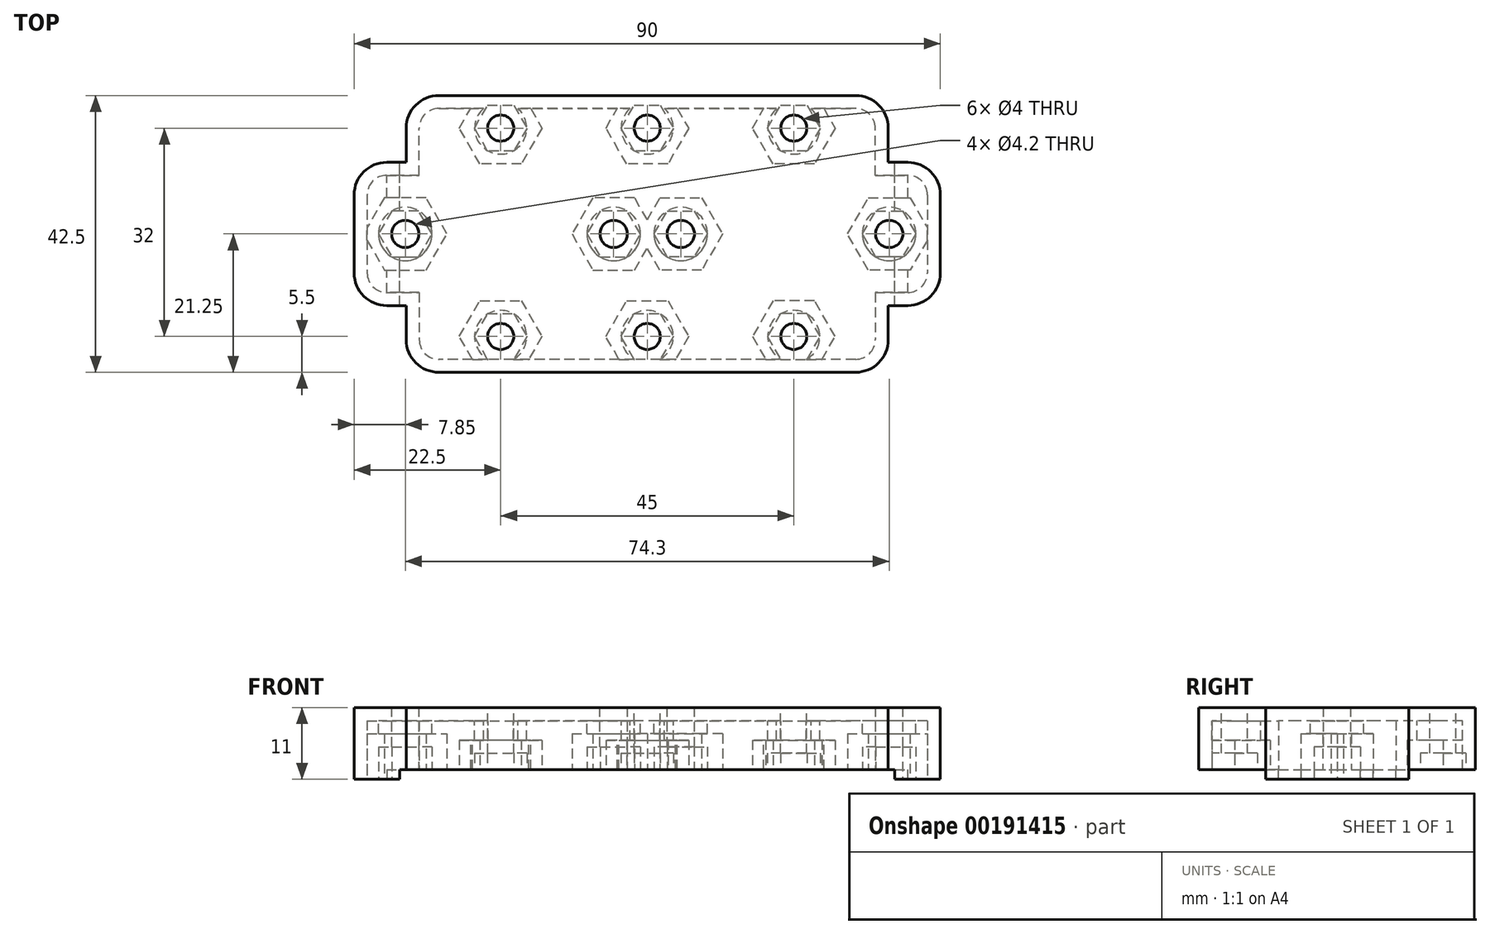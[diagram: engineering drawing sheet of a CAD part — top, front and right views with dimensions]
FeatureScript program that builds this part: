
annotation { "Feature Type Name" : "Feature", "Feature Type Description" : "" }
export const myFeature = defineFeature(function(context is Context, id is Id, definition is map)
    precondition{}
    {
        {
            var Q0;
            Q0=qCreatedBy(makeId("Top.planeOp"),FACE);
            var sketch = newSketch(context, id + "F0", { "sketchPlane" : qUnion([Q0])});
            skLineSegment(sketch, "E0.top", {"start": v(37, -37.5) * mm, "end": v(-37, -37.5) * mm});
            skLineSegment(sketch, "E0.left", {"start": v(45, -5.25) * mm, "end": v(45, -27.25) * mm});
            skLineSegment(sketch, "E0.right", {"start": v(-45, -5.25) * mm, "end": v(-45, -27.25) * mm});
            skPoint(sketch, "E0.middle", {"position": v(0, 0) * mm});
            skLineSegment(sketch, "E1", {"start": v(-37, 5) * mm, "end": v(37, 5) * mm});
            skPoint(sketch, "E0.bottom.end.orphan", {"position": v(-45, 37.5) * mm});
            skPoint(sketch, "E2.orphan", {"position": v(45, 37.5) * mm});
            skLineSegment(sketch, "E3.top", {"start": v(45, -5.25) * mm, "end": v(37, -5.25) * mm});
            skLineSegment(sketch, "E3.right", {"start": v(37, 5) * mm, "end": v(37, -5.25) * mm});
            skLineSegment(sketch, "E4", {"start": v(-45, -16.25) * mm, "end": v(45, -16.25) * mm, "construction": true});
            skLineSegment(sketch, "E5.MirrorCS", {"start": v(45, -27.25) * mm, "end": v(37, -27.25) * mm});
            skLineSegment(sketch, "E6.MirrorCS", {"start": v(37, -37.5) * mm, "end": v(37, -27.25) * mm});
            skLineSegment(sketch, "E7.MirrorCS", {"start": v(-45, -27.25) * mm, "end": v(-37, -27.25) * mm});
            skLineSegment(sketch, "E8.MirrorCS", {"start": v(-37, 5) * mm, "end": v(-37, -5.25) * mm});
            skLineSegment(sketch, "E9.MirrorCS", {"start": v(-45, -5.25) * mm, "end": v(-37, -5.25) * mm});
            skLineSegment(sketch, "E10.MirrorCS", {"start": v(-37, -37.5) * mm, "end": v(-37, -27.25) * mm});
            skPoint(sketch, "E11.orphan", {"position": v(45, 5) * mm});
            skPoint(sketch, "E12.MirrorCS.start.orphan", {"position": v(45, -37.5) * mm});
            skPoint(sketch, "E13.MirrorCS.start.orphan", {"position": v(-45, 5) * mm});
            skPoint(sketch, "E14.orphan", {"position": v(-45, -37.5) * mm});
            skSolve(sketch);
        }
        {
            var Q0;
            Q0=qSketchRegion(id+"F0",true);
            extrude(context, id + "F1", {"entities" : qUnion([Q0]), "depth" : 11 * mm});
        }
        {
            var Q0;
            {var subQ0=sQuery(id+"Ftu9CyJNp9XUoHb_1.wireOp",EDGE,"RhgawOvt-7kr6-Sdrn-dJV1-QJA8v9KPNXqK");var subQ1=sQuery(id+"FDzObh8OvUh78c8_1.wireOp",EDGE,"89ed7744-1fdc-4696-88ab-c0afdf2aee140.MirrorC");var subQ2=sQuery(id+"Ftu9CyJNp9XUoHb_1.wireOp",EDGE,"5e429970-d295-4fee-98a3-73d9fe4554250.MirrorC");var subQ3=sQuery(id+"FDzObh8OvUh78c8_1.wireOp",EDGE,"xi41FaaG-PnNu-ulyK-8lT2-qR5dbplvMgDO");var subQ4=sQuery(id+"F0.wireOp",EDGE,"E0.right");var subQ5=sQuery(id+"F0.wireOp",EDGE,"E0.left");Q0=makeQuery(id+"FwhSho8yxuuqSUd_1.boolean.opBoolean","SPLIT",FACE,{"disambiguationData":[TD([makeQuery(id+"F1.opExtrude","SWEPT_FACE",FACE,{"disambiguationData":[OSD([subQ5])]}),makeQuery(id+"F1.opExtrude","SWEPT_FACE",FACE,{"disambiguationData":[OSD([subQ4])]}),makeQuery(id+"FezKC2GjwbwwqvD_1.boolean.opBoolean","COPY",FACE,{"derivedFrom":makeQuery(id+"FezKC2GjwbwwqvD_1.opExtrude","SWEPT_FACE",FACE,{"disambiguationData":[OSD([subQ3])]})}),makeQuery(id+"FezKC2GjwbwwqvD_1.boolean.opBoolean","COPY",FACE,{"derivedFrom":makeQuery(id+"FezKC2GjwbwwqvD_1.opExtrude","CAP_FACE",FACE,{"disambiguationData":[OSD([subQ3])],"isStart":true})}),makeQuery(id+"FezKC2GjwbwwqvD_1.boolean.opBoolean","COPY",FACE,{"derivedFrom":makeQuery(id+"FezKC2GjwbwwqvD_1.opExtrude","CAP_FACE",FACE,{"disambiguationData":[OSD([subQ3])],"isStart":false})}),makeQuery(id+"FezKC2GjwbwwqvD_1.boolean.opBoolean","COPY",FACE,{"derivedFrom":makeQuery(id+"FezKC2GjwbwwqvD_1.opExtrude","SWEPT_FACE",FACE,{"disambiguationData":[OSD([subQ1])]})}),makeQuery(id+"FezKC2GjwbwwqvD_1.boolean.opBoolean","COPY",FACE,{"derivedFrom":makeQuery(id+"FezKC2GjwbwwqvD_1.opExtrude","CAP_FACE",FACE,{"disambiguationData":[OSD([subQ1])],"isStart":true})}),makeQuery(id+"FezKC2GjwbwwqvD_1.boolean.opBoolean","COPY",FACE,{"derivedFrom":makeQuery(id+"FezKC2GjwbwwqvD_1.opExtrude","CAP_FACE",FACE,{"disambiguationData":[OSD([subQ1])],"isStart":false})}),makeQuery(id+"Fv9pJnclqYY7mwX_1.boolean.opBoolean","COPY",FACE,{"derivedFrom":makeQuery(id+"Fv9pJnclqYY7mwX_1.opExtrude","SWEPT_FACE",FACE,{"disambiguationData":[OSD([subQ0])]})}),makeQuery(id+"Fv9pJnclqYY7mwX_1.boolean.opBoolean","COPY",FACE,{"derivedFrom":makeQuery(id+"Fv9pJnclqYY7mwX_1.opExtrude","CAP_FACE",FACE,{"disambiguationData":[OSD([subQ0])],"isStart":true})}),makeQuery(id+"Fv9pJnclqYY7mwX_1.boolean.opBoolean","COPY",FACE,{"derivedFrom":makeQuery(id+"Fv9pJnclqYY7mwX_1.opExtrude","CAP_FACE",FACE,{"disambiguationData":[OSD([subQ0])],"isStart":false})}),makeQuery(id+"Fv9pJnclqYY7mwX_1.boolean.opBoolean","COPY",FACE,{"derivedFrom":makeQuery(id+"Fv9pJnclqYY7mwX_1.opExtrude","SWEPT_FACE",FACE,{"disambiguationData":[OSD([subQ2])]})}),makeQuery(id+"Fv9pJnclqYY7mwX_1.boolean.opBoolean","COPY",FACE,{"derivedFrom":makeQuery(id+"Fv9pJnclqYY7mwX_1.opExtrude","CAP_FACE",FACE,{"disambiguationData":[OSD([subQ2])],"isStart":true})}),makeQuery(id+"Fv9pJnclqYY7mwX_1.boolean.opBoolean","COPY",FACE,{"derivedFrom":makeQuery(id+"Fv9pJnclqYY7mwX_1.opExtrude","CAP_FACE",FACE,{"disambiguationData":[OSD([subQ2])],"isStart":false})}),makeQuery(id+"FwhSho8yxuuqSUd_1.opExtrude","SWEPT_FACE",FACE,{"disambiguationData":[OSD([sQuery(id+"FwmFuU8kyHScjr7_1.wireOp",EDGE,"tpYNRhvY-wzzr-XPzG-ht9J-7hpqiQNTNnZq")])]}),makeQuery(id+"FwhSho8yxuuqSUd_1.opExtrude","SWEPT_FACE",FACE,{"disambiguationData":[OSD([sQuery(id+"FwmFuU8kyHScjr7_1.wireOp",EDGE,"4b7efacd-c033-4760-b56c-52784860be010.MirrorC")])]})])],"derivedFrom":makeQuery(id+"F1.opExtrude","CAP_FACE",FACE,{"disambiguationData":[OSD([sQuery(id+"F0.wireOp",EDGE,"E0.bottom"),sQuery(id+"F0.wireOp",EDGE,"E0.top"),subQ5,subQ4])],"isStart":false})});}
            var sketch = newSketch(context, id + "F2", { "sketchPlane" : qUnion([Q0])});
            skCircle(sketch, "E15", {"center": v(0, -32) * mm, "radius": 2 * mm});
            skCircle(sketch, "E16.MirrorC", {"center": v(-22.5, -32) * mm, "radius": 2 * mm});
            skCircle(sketch, "E17.MirrorC", {"center": v(22.5, -32) * mm, "radius": 2 * mm});
            skLineSegment(sketch, "E18", {"start": v(-45.52, -16) * mm, "end": v(58.52, -16) * mm});
            skCircle(sketch, "E19.MirrorC", {"center": v(-22.5, 0) * mm, "radius": 2 * mm});
            skCircle(sketch, "E20.MirrorC", {"center": v(0, 0) * mm, "radius": 2 * mm});
            skCircle(sketch, "E21.MirrorC", {"center": v(22.5, 0) * mm, "radius": 2 * mm});
            skSolve(sketch);
        }
        {
            var Q0;
            Q0=qSketchRegion(id+"F2",true);
            extrude(context, id + "F3", {"entities" : qUnion([Q0]), "operationType" : NewBodyOperationType.REMOVE, "endBound" : BoundingType.THROUGH_ALL, "oppositeDirection" : true, "depth" : 25 * mm});
        }
        {
            var Q0;
            Q0=makeQuery(id+"F1.opExtrude","CAP_FACE",FACE,{"disambiguationData":[OSD([sQuery(id+"F0.wireOp",EDGE,"E0.bottom"),sQuery(id+"F0.wireOp",EDGE,"E0.top"),sQuery(id+"F0.wireOp",EDGE,"E0.left"),sQuery(id+"F0.wireOp",EDGE,"E0.right")])],"isStart":true});
            var sketch = newSketch(context, id + "F4", { "sketchPlane" : qUnion([Q0])});
            skCircle(sketch, "E22.cCircle", {"center": v(-22.5, 32) * mm, "radius": 3.5 * mm, "construction": true});
            skLineSegment(sketch, "E22.0", {"start": v(-24.52, 35.5) * mm, "end": v(-20.48, 35.5) * mm});
            skLineSegment(sketch, "E22.1", {"start": v(-20.48, 35.5) * mm, "end": v(-18.46, 32) * mm});
            skLineSegment(sketch, "E22.2", {"start": v(-18.46, 32) * mm, "end": v(-20.48, 28.5) * mm});
            skLineSegment(sketch, "E22.3", {"start": v(-20.48, 28.5) * mm, "end": v(-24.52, 28.5) * mm});
            skLineSegment(sketch, "E22.4", {"start": v(-24.52, 28.5) * mm, "end": v(-26.54, 32) * mm});
            skLineSegment(sketch, "E22.5", {"start": v(-26.54, 32) * mm, "end": v(-24.52, 35.5) * mm});
            skPoint(sketch, "E22.0.midPoint", {"position": v(-22.5, 35.5) * mm});
            skLineSegment(sketch, "E23.MirrorCS", {"start": v(24.52, 35.5) * mm, "end": v(20.48, 35.5) * mm});
            skLineSegment(sketch, "E24.MirrorCS", {"start": v(26.54, 32) * mm, "end": v(24.52, 35.5) * mm});
            skLineSegment(sketch, "E25.MirrorCS", {"start": v(20.48, 28.5) * mm, "end": v(24.52, 28.5) * mm});
            skLineSegment(sketch, "E26.MirrorCS", {"start": v(18.46, 32) * mm, "end": v(20.48, 28.5) * mm});
            skCircle(sketch, "E27.MirrorC", {"center": v(22.5, 32) * mm, "radius": 3.5 * mm, "construction": true});
            skPoint(sketch, "E28.MirrorP", {"position": v(22.5, 35.5) * mm});
            skLineSegment(sketch, "E29.MirrorCS", {"start": v(24.52, 28.5) * mm, "end": v(26.54, 32) * mm});
            skLineSegment(sketch, "E30.MirrorCS", {"start": v(20.48, 35.5) * mm, "end": v(18.46, 32) * mm});
            skCircle(sketch, "E31.cCircle", {"center": v(0, 32) * mm, "radius": 3.5 * mm, "construction": true});
            skLineSegment(sketch, "E31.0", {"start": v(-2.02, 35.5) * mm, "end": v(2.02, 35.5) * mm});
            skLineSegment(sketch, "E31.1", {"start": v(2.02, 35.5) * mm, "end": v(4.04, 32) * mm});
            skLineSegment(sketch, "E31.2", {"start": v(4.04, 32) * mm, "end": v(2.02, 28.5) * mm});
            skLineSegment(sketch, "E31.3", {"start": v(2.02, 28.5) * mm, "end": v(-2.02, 28.5) * mm});
            skLineSegment(sketch, "E31.4", {"start": v(-2.02, 28.5) * mm, "end": v(-4.04, 32) * mm});
            skLineSegment(sketch, "E31.5", {"start": v(-4.04, 32) * mm, "end": v(-2.02, 35.5) * mm});
            skPoint(sketch, "E31.0.midPoint", {"position": v(0, 35.5) * mm});
            skCircle(sketch, "E32.cCircle", {"center": v(-22.5, 0) * mm, "radius": 3.5 * mm, "construction": true});
            skLineSegment(sketch, "E32.0", {"start": v(-24.52, 3.5) * mm, "end": v(-20.48, 3.5) * mm});
            skLineSegment(sketch, "E32.1", {"start": v(-20.48, 3.5) * mm, "end": v(-18.46, 0) * mm});
            skLineSegment(sketch, "E32.2", {"start": v(-18.46, 0) * mm, "end": v(-20.48, -3.5) * mm});
            skLineSegment(sketch, "E32.3", {"start": v(-20.48, -3.5) * mm, "end": v(-24.52, -3.5) * mm});
            skLineSegment(sketch, "E32.4", {"start": v(-24.52, -3.5) * mm, "end": v(-26.54, 0) * mm});
            skLineSegment(sketch, "E32.5", {"start": v(-26.54, 0) * mm, "end": v(-24.52, 3.5) * mm});
            skPoint(sketch, "E32.0.midPoint", {"position": v(-22.5, 3.5) * mm});
            skCircle(sketch, "E33.cCircle", {"center": v(0, 0) * mm, "radius": 3.5 * mm, "construction": true});
            skLineSegment(sketch, "E33.0", {"start": v(-2.02, 3.5) * mm, "end": v(2.02, 3.5) * mm});
            skLineSegment(sketch, "E33.1", {"start": v(2.02, 3.5) * mm, "end": v(4.04, 0) * mm});
            skLineSegment(sketch, "E33.2", {"start": v(4.04, 0) * mm, "end": v(2.02, -3.5) * mm});
            skLineSegment(sketch, "E33.3", {"start": v(2.02, -3.5) * mm, "end": v(-2.02, -3.5) * mm});
            skLineSegment(sketch, "E33.4", {"start": v(-2.02, -3.5) * mm, "end": v(-4.04, 0) * mm});
            skLineSegment(sketch, "E33.5", {"start": v(-4.04, 0) * mm, "end": v(-2.02, 3.5) * mm});
            skPoint(sketch, "E33.0.midPoint", {"position": v(0, 3.5) * mm});
            skCircle(sketch, "E34.cCircle", {"center": v(22.5, 0) * mm, "radius": 3.5 * mm, "construction": true});
            skLineSegment(sketch, "E34.0", {"start": v(20.48, 3.5) * mm, "end": v(24.52, 3.5) * mm});
            skLineSegment(sketch, "E34.1", {"start": v(24.52, 3.5) * mm, "end": v(26.54, 0) * mm});
            skLineSegment(sketch, "E34.2", {"start": v(26.54, 0) * mm, "end": v(24.52, -3.5) * mm});
            skLineSegment(sketch, "E34.3", {"start": v(24.52, -3.5) * mm, "end": v(20.48, -3.5) * mm});
            skLineSegment(sketch, "E34.4", {"start": v(20.48, -3.5) * mm, "end": v(18.46, 0) * mm});
            skLineSegment(sketch, "E34.5", {"start": v(18.46, 0) * mm, "end": v(20.48, 3.5) * mm});
            skPoint(sketch, "E34.0.midPoint", {"position": v(22.5, 3.5) * mm});
            skSolve(sketch);
        }
        {
            var Q0;
            Q0=qSketchRegion(id+"F4",true);
            extrude(context, id + "F5", {"entities" : qUnion([Q0]), "operationType" : NewBodyOperationType.REMOVE, "oppositeDirection" : true, "depth" : 4 * mm});
        }
        {
            var Q0;
            Q0=makeQuery(id+"F1.opExtrude","CAP_FACE",FACE,{"disambiguationData":[OSD([sQuery(id+"F0.wireOp",EDGE,"E0.top"),sQuery(id+"F0.wireOp",EDGE,"E0.left"),sQuery(id+"F0.wireOp",EDGE,"E0.right"),sQuery(id+"F0.wireOp",EDGE,"E1")])],"isStart":true});
            var sketch = newSketch(context, id + "F6", { "sketchPlane" : qUnion([Q0])});
            skLineSegment(sketch, "E35.bottom", {"start": v(38, 37.5) * mm, "end": v(-38, 37.5) * mm});
            skLineSegment(sketch, "E35.top", {"start": v(38, -5) * mm, "end": v(-38, -5) * mm});
            skLineSegment(sketch, "E35.left", {"start": v(38, 37.5) * mm, "end": v(38, -5) * mm});
            skLineSegment(sketch, "E35.right", {"start": v(-38, 37.5) * mm, "end": v(-38, -5) * mm});
            skPoint(sketch, "E35.middle", {"position": v(0, 16.25) * mm});
            skSolve(sketch);
        }
        {
            var Q0;
            Q0 = qSketchRegion(id + "F6", true);
            extrude(context, id + "F7", {"entities" : qUnion([Q0]), "operationType" : NewBodyOperationType.REMOVE, "oppositeDirection" : true, "depth" : 1.5 * mm});
        }
        {
            var Q0;
            Q0=makeQuery(id+"F1.opExtrude","SWEPT_EDGE",EDGE,{"disambiguationData":[OSD([sQuery(id+"F0.wireOp",EDGE,"E0.top"),sQuery(id+"F0.wireOp",EDGE,"E10.MirrorCS")])]});
            var Q1;
            Q1=makeQuery(id+"F1.opExtrude","SWEPT_EDGE",EDGE,{"disambiguationData":[OSD([sQuery(id+"F0.wireOp",EDGE,"E7.MirrorCS"),sQuery(id+"F0.wireOp",EDGE,"E0.right")])]});
            var Q2;
            Q2=makeQuery(id+"F1.opExtrude","SWEPT_EDGE",EDGE,{"disambiguationData":[OSD([sQuery(id+"F0.wireOp",EDGE,"E9.MirrorCS"),sQuery(id+"F0.wireOp",EDGE,"E0.right")])]});
            var Q3;
            Q3=makeQuery(id+"F1.opExtrude","SWEPT_EDGE",EDGE,{"disambiguationData":[OSD([sQuery(id+"F0.wireOp",EDGE,"E1"),sQuery(id+"F0.wireOp",EDGE,"E8.MirrorCS")])]});
            var Q4;
            Q4=makeQuery(id+"F1.opExtrude","SWEPT_EDGE",EDGE,{"disambiguationData":[OSD([sQuery(id+"F0.wireOp",EDGE,"E1"),sQuery(id+"F0.wireOp",EDGE,"E3.right")])]});
            var Q5;
            Q5=makeQuery(id+"F1.opExtrude","SWEPT_EDGE",EDGE,{"disambiguationData":[OSD([sQuery(id+"F0.wireOp",EDGE,"E0.left"),sQuery(id+"F0.wireOp",EDGE,"E3.top")])]});
            var Q6;
            Q6=makeQuery(id+"F1.opExtrude","SWEPT_EDGE",EDGE,{"disambiguationData":[OSD([sQuery(id+"F0.wireOp",EDGE,"E0.top"),sQuery(id+"F0.wireOp",EDGE,"E6.MirrorCS")])]});
            var Q7;
            Q7=makeQuery(id+"F1.opExtrude","SWEPT_EDGE",EDGE,{"disambiguationData":[OSD([sQuery(id+"F0.wireOp",EDGE,"E0.left"),sQuery(id+"F0.wireOp",EDGE,"E5.MirrorCS")])]});
            fillet(context, id + "F8", {"entities" : qUnion([Q0, Q1, Q2, Q3, Q4, Q5, Q6, Q7]), "radius" : 5 * mm, "tangentPropagation" : true, "allowEdgeOverflow" : false});
        }
        {
            var Q0;
            Q0=makeQuery(id+"F1.opExtrude","CAP_FACE",FACE,{"disambiguationData":[OSD([sQuery(id+"F0.wireOp",EDGE,"E0.top"),sQuery(id+"F0.wireOp",EDGE,"E0.left"),sQuery(id+"F0.wireOp",EDGE,"E1"),sQuery(id+"F0.wireOp",EDGE,"E3.top"),sQuery(id+"F0.wireOp",EDGE,"E3.right"),sQuery(id+"F0.wireOp",EDGE,"E5.MirrorCS"),sQuery(id+"F0.wireOp",EDGE,"E6.MirrorCS"),sQuery(id+"F0.wireOp",EDGE,"E7.MirrorCS"),sQuery(id+"F0.wireOp",EDGE,"E8.MirrorCS"),sQuery(id+"F0.wireOp",EDGE,"E9.MirrorCS"),sQuery(id+"F0.wireOp",EDGE,"E0.right"),sQuery(id+"F0.wireOp",EDGE,"E10.MirrorCS")])],"isStart":false});
            var sketch = newSketch(context, id + "F9", { "sketchPlane" : qUnion([Q0])});
            skPoint(sketch, "E36.middle", {"position": v(21.15, -16.25) * mm});
            skLineSegment(sketch, "E37", {"start": v(-45, -16.25) * mm, "end": v(54.06, -16.25) * mm, "construction": true});
            skPoint(sketch, "E38", {"position": v(45, -16.25) * mm});
            skCircle(sketch, "E39", {"center": v(37.15, -16.25) * mm, "radius": 2.1 * mm});
            skLineSegment(sketch, "E40", {"start": v(21.15, -16.25) * mm, "end": v(21.15, -48.47) * mm, "construction": true});
            skCircle(sketch, "E41.MirrorC", {"center": v(5.15, -16.25) * mm, "radius": 2.1 * mm});
            skLineSegment(sketch, "E42.MirrorCS", {"start": v(45, -16.25) * mm, "end": v(-54.06, -16.25) * mm, "construction": true});
            skCircle(sketch, "E43.MirrorC", {"center": v(-37.15, -16.25) * mm, "radius": 2.1 * mm});
            skPoint(sketch, "E44.MirrorP", {"position": v(-21.15, -16.25) * mm});
            skPoint(sketch, "E45.MirrorP", {"position": v(-45, -16.25) * mm});
            skLineSegment(sketch, "E46.MirrorCS", {"start": v(-21.15, -16.25) * mm, "end": v(-21.15, -48.47) * mm, "construction": true});
            skCircle(sketch, "E47.MirrorC", {"center": v(-5.15, -16.25) * mm, "radius": 2.1 * mm});
            skSolve(sketch);
        }
        {
            var Q0;
            Q0 = qSketchRegion(id + "F9", true);
            extrude(context, id + "F10", {"entities" : qUnion([Q0]), "operationType" : NewBodyOperationType.REMOVE, "endBound" : BoundingType.THROUGH_ALL, "oppositeDirection" : true, "depth" : 1 * mm});
        }
        {
            var Q0;
            {var subQ0=sQuery(id+"F0.wireOp",EDGE,"E7.MirrorCS");var subQ1=sQuery(id+"F0.wireOp",EDGE,"E9.MirrorCS");var subQ2=sQuery(id+"F0.wireOp",EDGE,"E0.right");Q0=makeQuery(id+"F7.boolean.opBoolean","SPLIT",FACE,{"disambiguationData":[TD([makeQuery(id+"F1.opExtrude","SWEPT_FACE",FACE,{"disambiguationData":[OSD([subQ0])]})])],"derivedFrom":makeQuery(id+"F1.opExtrude","CAP_FACE",FACE,{"disambiguationData":[OSD([sQuery(id+"F0.wireOp",EDGE,"E0.top"),sQuery(id+"F0.wireOp",EDGE,"E0.left"),sQuery(id+"F0.wireOp",EDGE,"E1"),sQuery(id+"F0.wireOp",EDGE,"E3.top"),sQuery(id+"F0.wireOp",EDGE,"E3.right"),sQuery(id+"F0.wireOp",EDGE,"E5.MirrorCS"),sQuery(id+"F0.wireOp",EDGE,"E6.MirrorCS"),subQ0,sQuery(id+"F0.wireOp",EDGE,"E8.MirrorCS"),subQ1,subQ2,sQuery(id+"F0.wireOp",EDGE,"E10.MirrorCS")])],"isStart":true})});}
            var sketch = newSketch(context, id + "F11", { "sketchPlane" : qUnion([Q0])});
            skCircle(sketch, "E48.cCircle", {"center": v(-37.15, 16.25) * mm, "radius": 3.55 * mm, "construction": true});
            skLineSegment(sketch, "E48.0", {"start": v(-39.2, 19.8) * mm, "end": v(-35.1, 19.8) * mm});
            skLineSegment(sketch, "E48.1", {"start": v(-35.1, 19.8) * mm, "end": v(-33.05, 16.25) * mm});
            skLineSegment(sketch, "E48.2", {"start": v(-33.05, 16.25) * mm, "end": v(-35.1, 12.7) * mm});
            skLineSegment(sketch, "E48.3", {"start": v(-35.1, 12.7) * mm, "end": v(-39.2, 12.7) * mm});
            skLineSegment(sketch, "E48.4", {"start": v(-39.2, 12.7) * mm, "end": v(-41.25, 16.25) * mm});
            skLineSegment(sketch, "E48.5", {"start": v(-41.25, 16.25) * mm, "end": v(-39.2, 19.8) * mm});
            skPoint(sketch, "E48.0.midPoint", {"position": v(-37.15, 19.8) * mm});
            skCircle(sketch, "E49.cCircle", {"center": v(-5.15, 16.25) * mm, "radius": 3.55 * mm, "construction": true});
            skLineSegment(sketch, "E49.0", {"start": v(-7.2, 19.8) * mm, "end": v(-3.1, 19.8) * mm});
            skLineSegment(sketch, "E49.1", {"start": v(-3.1, 19.8) * mm, "end": v(-1.05, 16.25) * mm});
            skLineSegment(sketch, "E49.2", {"start": v(-1.05, 16.25) * mm, "end": v(-3.1, 12.7) * mm});
            skLineSegment(sketch, "E49.3", {"start": v(-3.1, 12.7) * mm, "end": v(-7.2, 12.7) * mm});
            skLineSegment(sketch, "E49.4", {"start": v(-7.2, 12.7) * mm, "end": v(-9.25, 16.25) * mm});
            skLineSegment(sketch, "E49.5", {"start": v(-9.25, 16.25) * mm, "end": v(-7.2, 19.8) * mm});
            skPoint(sketch, "E49.0.midPoint", {"position": v(-5.15, 19.8) * mm});
            skLineSegment(sketch, "E50.MirrorCS", {"start": v(33.05, 16.25) * mm, "end": v(35.1, 12.7) * mm});
            skLineSegment(sketch, "E51.MirrorCS", {"start": v(3.1, 19.8) * mm, "end": v(1.05, 16.25) * mm});
            skLineSegment(sketch, "E52.MirrorCS", {"start": v(41.25, 16.25) * mm, "end": v(39.2, 19.8) * mm});
            skLineSegment(sketch, "E53.MirrorCS", {"start": v(39.2, 12.7) * mm, "end": v(41.25, 16.25) * mm});
            skLineSegment(sketch, "E54.MirrorCS", {"start": v(39.2, 19.8) * mm, "end": v(35.1, 19.8) * mm});
            skLineSegment(sketch, "E55.MirrorCS", {"start": v(7.2, 19.8) * mm, "end": v(3.1, 19.8) * mm});
            skPoint(sketch, "E56.MirrorP", {"position": v(37.15, 19.8) * mm});
            skCircle(sketch, "E57.MirrorC", {"center": v(37.15, 16.25) * mm, "radius": 3.55 * mm, "construction": true});
            skLineSegment(sketch, "E58.MirrorCS", {"start": v(9.25, 16.25) * mm, "end": v(7.2, 19.8) * mm});
            skCircle(sketch, "E59.MirrorC", {"center": v(5.15, 16.25) * mm, "radius": 3.55 * mm, "construction": true});
            skLineSegment(sketch, "E60.MirrorCS", {"start": v(7.2, 12.7) * mm, "end": v(9.25, 16.25) * mm});
            skLineSegment(sketch, "E61.MirrorCS", {"start": v(35.1, 12.7) * mm, "end": v(39.2, 12.7) * mm});
            skLineSegment(sketch, "E62.MirrorCS", {"start": v(35.1, 19.8) * mm, "end": v(33.05, 16.25) * mm});
            skPoint(sketch, "E63.MirrorP", {"position": v(5.15, 19.8) * mm});
            skLineSegment(sketch, "E64.MirrorCS", {"start": v(3.1, 12.7) * mm, "end": v(7.2, 12.7) * mm});
            skLineSegment(sketch, "E65.MirrorCS", {"start": v(1.05, 16.25) * mm, "end": v(3.1, 12.7) * mm});
            skSolve(sketch);
        }
        {
            var Q0;
            Q0 = qSketchRegion(id + "F11", true);
            extrude(context, id + "F12", {"entities" : qUnion([Q0]), "operationType" : NewBodyOperationType.REMOVE, "oppositeDirection" : true, "depth" : 5 * mm});
        }
        {
            var Q0;
            Q0=makeQuery(id+"F7.boolean.opBoolean","COPY",FACE,{"derivedFrom":makeQuery(id+"F7.opExtrude","CAP_FACE",FACE,{"disambiguationData":[OSD([sQuery(id+"F6.wireOp",EDGE,"E35.bottom"),sQuery(id+"F6.wireOp",EDGE,"E35.top"),sQuery(id+"F6.wireOp",EDGE,"E35.left"),sQuery(id+"F6.wireOp",EDGE,"E35.right")])],"isStart":false})});
            var Q1;
            {var subQ0=sQuery(id+"F0.wireOp",EDGE,"E7.MirrorCS");var subQ1=sQuery(id+"F0.wireOp",EDGE,"E9.MirrorCS");var subQ2=sQuery(id+"F0.wireOp",EDGE,"E0.right");Q1=makeQuery(id+"F7.boolean.opBoolean","SPLIT",FACE,{"disambiguationData":[TD([makeQuery(id+"F1.opExtrude","SWEPT_FACE",FACE,{"disambiguationData":[OSD([subQ0])]})])],"derivedFrom":makeQuery(id+"F1.opExtrude","CAP_FACE",FACE,{"disambiguationData":[OSD([sQuery(id+"F0.wireOp",EDGE,"E0.top"),sQuery(id+"F0.wireOp",EDGE,"E0.left"),sQuery(id+"F0.wireOp",EDGE,"E1"),sQuery(id+"F0.wireOp",EDGE,"E3.top"),sQuery(id+"F0.wireOp",EDGE,"E3.right"),sQuery(id+"F0.wireOp",EDGE,"E5.MirrorCS"),sQuery(id+"F0.wireOp",EDGE,"E6.MirrorCS"),subQ0,sQuery(id+"F0.wireOp",EDGE,"E8.MirrorCS"),subQ1,subQ2,sQuery(id+"F0.wireOp",EDGE,"E10.MirrorCS")])],"isStart":true})});}
            var Q2;
            {var subQ0=sQuery(id+"F0.wireOp",EDGE,"E0.left");var subQ1=sQuery(id+"F0.wireOp",EDGE,"E3.top");var subQ2=sQuery(id+"F0.wireOp",EDGE,"E5.MirrorCS");Q2=makeQuery(id+"F7.boolean.opBoolean","SPLIT",FACE,{"disambiguationData":[TD([makeQuery(id+"F1.opExtrude","SWEPT_FACE",FACE,{"disambiguationData":[OSD([subQ0])]})])],"derivedFrom":makeQuery(id+"F1.opExtrude","CAP_FACE",FACE,{"disambiguationData":[OSD([sQuery(id+"F0.wireOp",EDGE,"E0.top"),subQ0,sQuery(id+"F0.wireOp",EDGE,"E1"),subQ1,sQuery(id+"F0.wireOp",EDGE,"E3.right"),subQ2,sQuery(id+"F0.wireOp",EDGE,"E6.MirrorCS"),sQuery(id+"F0.wireOp",EDGE,"E7.MirrorCS"),sQuery(id+"F0.wireOp",EDGE,"E8.MirrorCS"),sQuery(id+"F0.wireOp",EDGE,"E9.MirrorCS"),sQuery(id+"F0.wireOp",EDGE,"E0.right"),sQuery(id+"F0.wireOp",EDGE,"E10.MirrorCS")])],"isStart":true})});}
            shell(context, id + "F13", {"entities" : qUnion([Q0, Q1, Q2]), "thickness" : 2 * mm});
        }
    });
